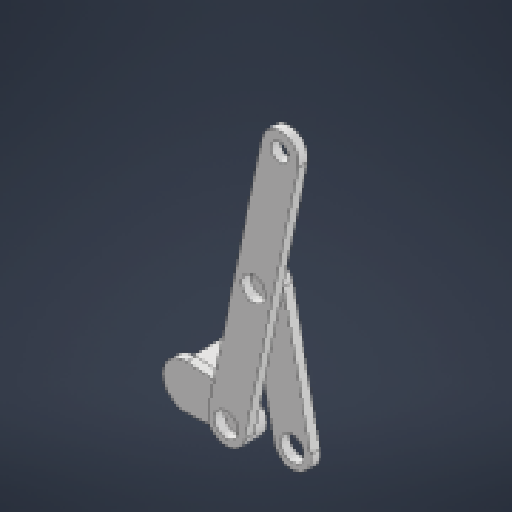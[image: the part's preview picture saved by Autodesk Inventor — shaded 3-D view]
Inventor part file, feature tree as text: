
AUTODESK INVENTOR PART (.ipt)
format: ipt  version: 2024.1 (Build 281209000, 209)  size: 242,688 bytes
history: native  units: in
note: dims shown in document units (in); Inventor stores cm internally (conversion verified against a paired STEP export)
features: extrude x8, sketch x5, projected_geometry x5, other x4, reference x3, chamfer x2
ambient origin geometry x8: Origin, YZ Plane, XZ Plane, XY Plane, X Axis, Y Axis, Z Axis, Center Point
bodies: Solid1 (feature_tree)
feature tree (27):
  sketch  "Sketch1"  dims[d0=0.25in d1=0.25in]
  extrude  "Extrusion1"  Depth=0.25in
  extrude  "Extrusion2"  Depth=0.0625in
  chamfer  "Chamfer1"  Distance=0.0625in
  extrude  "Extrusion3"  Depth=0.277in TaperAngle=0.0deg
  sketch  "Sketch3"  dims[d6=0.002in d7=0.277in d8=0.0in]
  extrude  "Extrusion4"  Depth=0.02in TaperAngle=0.0deg
  extrude  "Extrusion5"  Depth=0.15in
  extrude  "Extrusion6"  Depth=0.125in
  extrude  "Extrusion7"  Depth=0.125in
  extrude  "Extrusion8"  Depth=0.25in
  chamfer  "Chamfer2"  Distance=0.12in
  reference  "Reference1"
  reference  "Reference2"
  reference  "Reference3"
  sketch  "Sketch2"  dims[d2=0.25in d3=0.16in d4=0.0625in d5=0.0in]
  projected_geometry  "Projected Loop1"
  projected_geometry  "Projected Loop2"
  projected_geometry  "Projected Loop3"
  projected_geometry  "Projected Loop4"
  sketch  "Sketch4"  dims[d9=0.005in d10=0.125in d11=45.0deg d12=0.02in d13=0.0in]
  projected_geometry  "Projected Loop5"
  sketch  "Sketch5"  dims[d14=0.15in d15=0.15in d16=0.005in d17=0.005in d18=0.25in d20=0.12in d21=0.0625in d22=0.0in d23=0.008in d24=0.0in d25=0.0938in d26=0.0in d27=0.25in d28=0.25in d29=0.0233in d30=0.0in d31=0.12in d32=0.0in d33=0.0in d34=0.005in d35=0.125in d36=45.0deg]
  other  "<userpath>\Documents\School\FallCAD\Bio\Bio.iam"
  other  "Bio.iam"
  other  "Bio12tNew:1"
  other  "Alignment:1"
